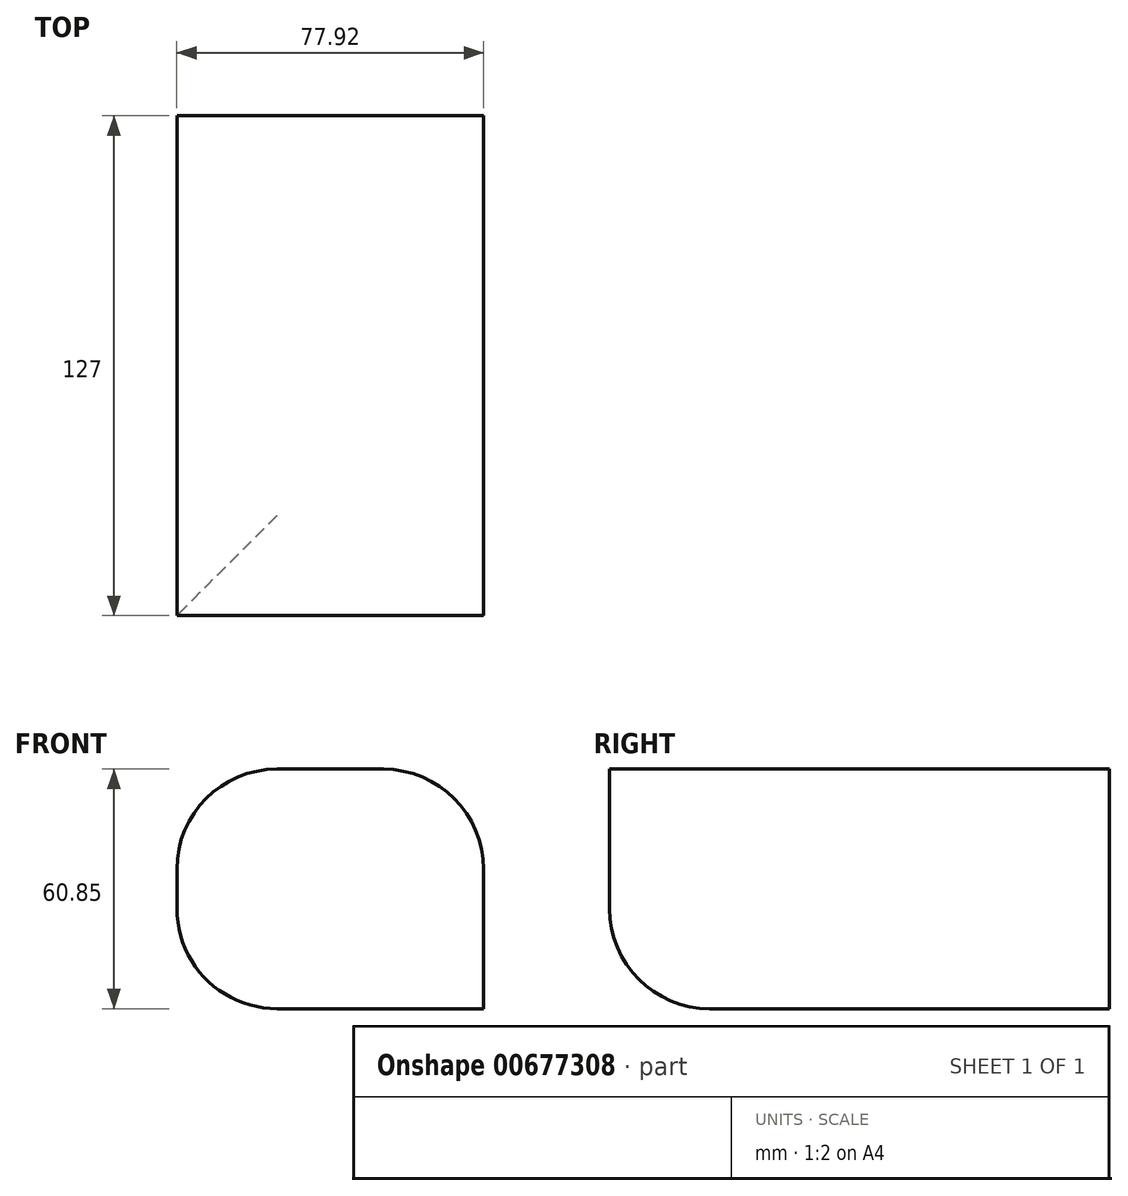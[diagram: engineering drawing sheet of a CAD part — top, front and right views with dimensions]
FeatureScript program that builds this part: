
annotation { "Feature Type Name" : "Feature", "Feature Type Description" : "" }
export const myFeature = defineFeature(function(context is Context, id is Id, definition is map)
    precondition{}
    {
        {
            var Q0;
            Q0=qCreatedBy(makeId("Front.planeOp"),FACE);
            var sketch = newSketch(context, id + "F0", { "sketchPlane" : qUnion([Q0])});
            skLineSegment(sketch, "E0.bottom", {"start": v(-48.46, -21.25) * mm, "end": v(29.46, -21.25) * mm});
            skLineSegment(sketch, "E0.top", {"start": v(-48.46, 39.6) * mm, "end": v(29.46, 39.6) * mm});
            skLineSegment(sketch, "E0.left", {"start": v(-48.46, -21.25) * mm, "end": v(-48.46, 39.6) * mm});
            skLineSegment(sketch, "E0.right", {"start": v(29.46, -21.25) * mm, "end": v(29.46, 39.6) * mm});
            skSolve(sketch);
        }
        {
            var Q0;
            Q0 = qSketchRegion(id + "F0", true);
            extrude(context, id + "F1", {"entities" : qUnion([Q0]), "depth" : 127 * mm, "offsetDistance" : 25.4 * mm});
        }
        {
            var Q0;
            Q0=makeQuery(id+"F1.opExtrude","SWEPT_EDGE",EDGE,{"disambiguationData":[OSD([sQuery(id+"F0.wireOp",EDGE,"E0.top"),sQuery(id+"F0.wireOp",EDGE,"E0.left")])]});
            var Q1;
            Q1=makeQuery(id+"F1.opExtrude","SWEPT_EDGE",EDGE,{"disambiguationData":[OSD([sQuery(id+"F0.wireOp",EDGE,"E0.top"),sQuery(id+"F0.wireOp",EDGE,"E0.right")])]});
            var Q2;
            Q2=makeQuery(id+"F1.opExtrude","CAP_EDGE",EDGE,{"disambiguationData":[OSD([sQuery(id+"F0.wireOp",EDGE,"E0.bottom")])],"isStart":false});
            var Q3;
            Q3=makeQuery(id+"F1.opExtrude","SWEPT_EDGE",EDGE,{"disambiguationData":[OSD([sQuery(id+"F0.wireOp",EDGE,"E0.bottom"),sQuery(id+"F0.wireOp",EDGE,"E0.left")])]});
            fillet(context, id + "F2", {"entities" : qUnion([Q0, Q1, Q2, Q3]), "radius" : 25.4 * mm, "tangentPropagation" : true, "allowEdgeOverflow" : false});
        }
    });
